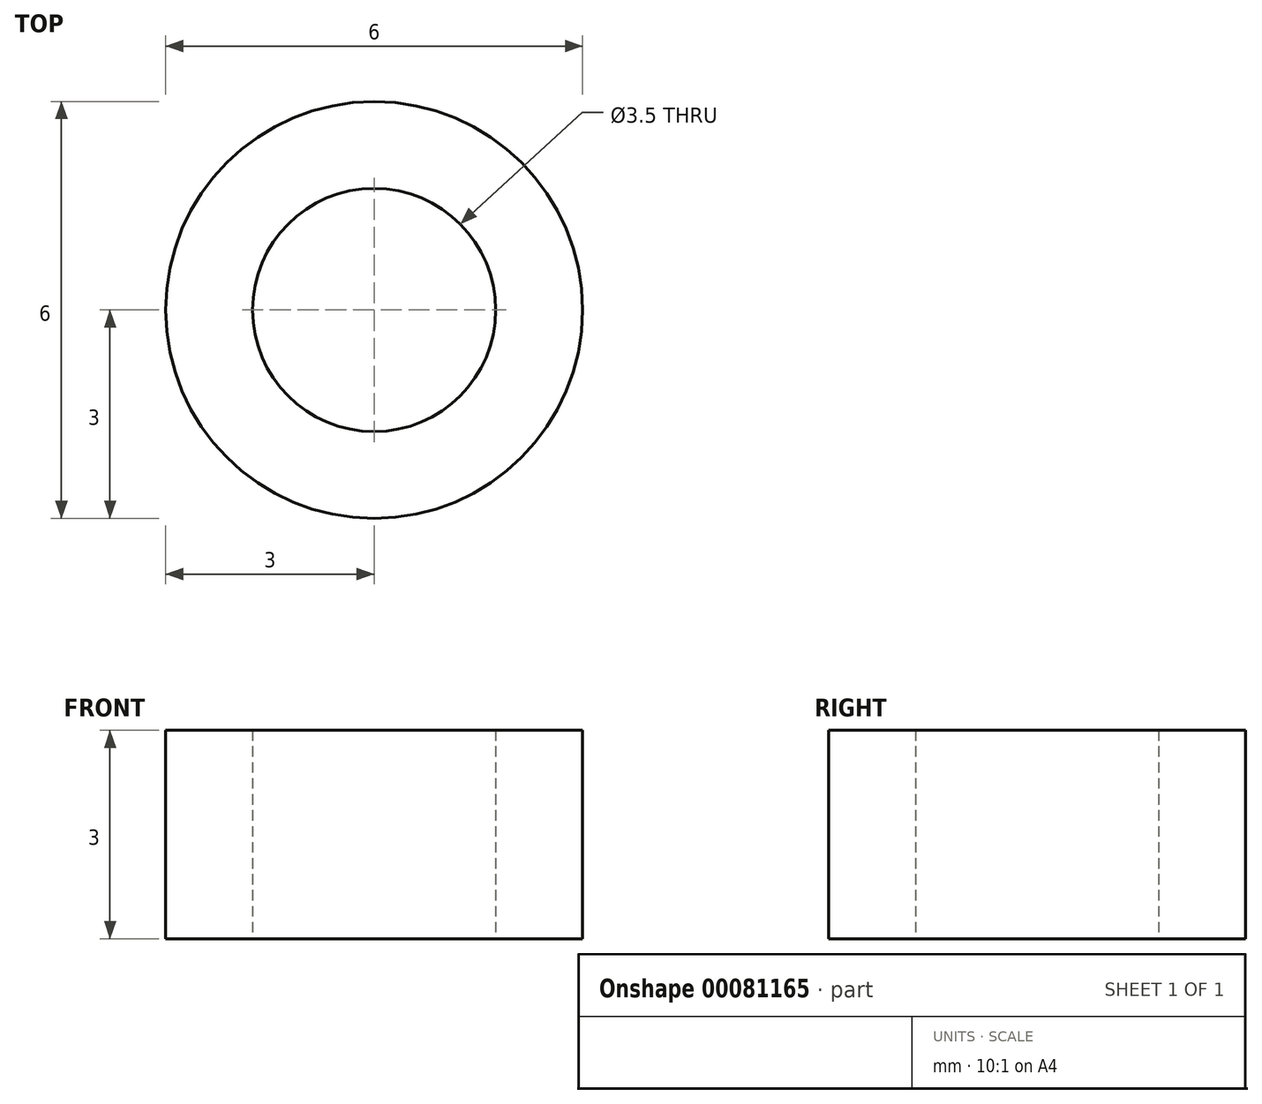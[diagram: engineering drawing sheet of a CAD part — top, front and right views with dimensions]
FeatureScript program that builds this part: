
annotation { "Feature Type Name" : "Feature", "Feature Type Description" : "" }
export const myFeature = defineFeature(function(context is Context, id is Id, definition is map)
    precondition{}
    {
        {
            var Q0;
            Q0=qCreatedBy(makeId("Top.planeOp"),FACE);
            var sketch = newSketch(context, id + "F0", { "sketchPlane" : qUnion([Q0])});
            skCircle(sketch, "E0", {"center": v(0, 0) * mm, "radius": 1.75 * mm});
            skCircle(sketch, "E1", {"center": v(0, 0) * mm, "radius": 3 * mm});
            skSolve(sketch);
        }
        {
            var Q0;
            Q0=qSketchRegion(id+"F0",true);
            extrude(context, id + "F1", {"entities" : qUnion([Q0]), "depth" : 3 * mm});
        }
    });
